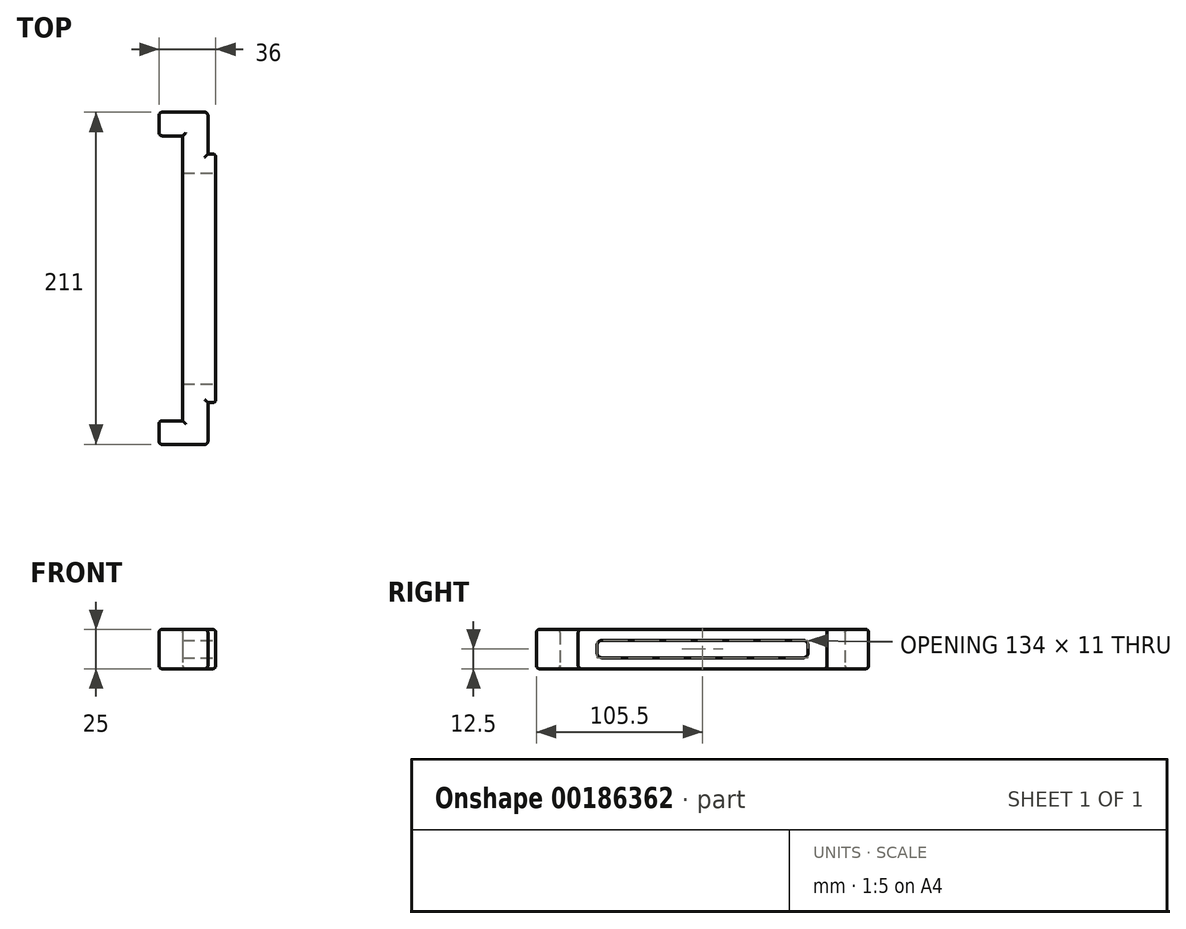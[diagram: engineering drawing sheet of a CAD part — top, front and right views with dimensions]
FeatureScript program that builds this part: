
annotation { "Feature Type Name" : "Feature", "Feature Type Description" : "" }
export const myFeature = defineFeature(function(context is Context, id is Id, definition is map)
    precondition{}
    {
        {
            var Q0;
            Q0=qCreatedBy(makeId("Top.planeOp"),FACE);
            var sketch = newSketch(context, id + "F0", { "sketchPlane" : qUnion([Q0])});
            skLineSegment(sketch, "E0", {"start": v(0, 90.5) * mm, "end": v(0, -90.5) * mm});
            skLineSegment(sketch, "E1", {"start": v(0, -90.5) * mm, "end": v(-15, -90.5) * mm});
            skLineSegment(sketch, "E2", {"start": v(-15, -90.5) * mm, "end": v(-15, -105.5) * mm});
            skLineSegment(sketch, "E3", {"start": v(-15, -105.5) * mm, "end": v(16, -105.5) * mm});
            skLineSegment(sketch, "E4", {"start": v(16, -105.5) * mm, "end": v(16, -79) * mm});
            skLineSegment(sketch, "E5", {"start": v(16, 105.5) * mm, "end": v(-15, 105.5) * mm});
            skLineSegment(sketch, "E6", {"start": v(-15, 105.5) * mm, "end": v(-15, 90.5) * mm});
            skLineSegment(sketch, "E7", {"start": v(-15, 90.5) * mm, "end": v(0, 90.5) * mm});
            skLineSegment(sketch, "E8", {"start": v(16, 79) * mm, "end": v(21, 79) * mm});
            skLineSegment(sketch, "E9", {"start": v(21, 79) * mm, "end": v(21, -79) * mm});
            skLineSegment(sketch, "E10", {"start": v(21, -79) * mm, "end": v(16, -79) * mm});
            skLineSegment(sketch, "E11.trimOffspring", {"start": v(16, 79) * mm, "end": v(16, 105.5) * mm});
            skSolve(sketch);
        }
        {
            var Q0;
            Q0=makeQuery(id+"F0.imprint","IMPRINT",FACE,{"disambiguationData":[TD([[makeQuery(id+"F0.imprint","IMPRINT",EDGE,{"derivedFrom":sQuery(id+"F0.wireOp",EDGE,"E0")}),1.0]])]});
            extrude(context, id + "F1", {"entities" : qUnion([Q0]), "depth" : 25 * mm});
        }
        {
            var Q0;
            Q0=makeQuery(id+"F1.opExtrude","SWEPT_EDGE",EDGE,{"disambiguationData":[OSD([sQuery(id+"F0.wireOp",EDGE,"E2"),sQuery(id+"F0.wireOp",EDGE,"E3")])]});
            var Q1;
            Q1=makeQuery(id+"F1.opExtrude","SWEPT_EDGE",EDGE,{"disambiguationData":[OSD([sQuery(id+"F0.wireOp",EDGE,"E5"),sQuery(id+"F0.wireOp",EDGE,"E6")])]});
            var Q2;
            Q2=makeQuery(id+"F1.opExtrude","SWEPT_EDGE",EDGE,{"disambiguationData":[OSD([sQuery(id+"F0.wireOp",EDGE,"E6"),sQuery(id+"F0.wireOp",EDGE,"E7")])]});
            var Q3;
            Q3=makeQuery(id+"F1.opExtrude","SWEPT_EDGE",EDGE,{"disambiguationData":[OSD([sQuery(id+"F0.wireOp",EDGE,"E1"),sQuery(id+"F0.wireOp",EDGE,"E2")])]});
            var Q4;
            Q4=makeQuery(id+"F1.opExtrude","SWEPT_EDGE",EDGE,{"disambiguationData":[OSD([sQuery(id+"F0.wireOp",EDGE,"E3"),sQuery(id+"F0.wireOp",EDGE,"E4")])]});
            var Q5;
            Q5=makeQuery(id+"F1.opExtrude","SWEPT_EDGE",EDGE,{"disambiguationData":[OSD([sQuery(id+"F0.wireOp",EDGE,"E9"),sQuery(id+"F0.wireOp",EDGE,"E10")])]});
            var Q6;
            Q6=makeQuery(id+"F1.opExtrude","SWEPT_EDGE",EDGE,{"disambiguationData":[OSD([sQuery(id+"F0.wireOp",EDGE,"E8"),sQuery(id+"F0.wireOp",EDGE,"E9")])]});
            var Q7;
            Q7=makeQuery(id+"F1.opExtrude","SWEPT_EDGE",EDGE,{"disambiguationData":[OSD([sQuery(id+"F0.wireOp",EDGE,"E5"),sQuery(id+"F0.wireOp",EDGE,"E11.trimOffspring")])]});
            fillet(context, id + "F2", {"entities" : qUnion([Q0, Q1, Q2, Q3, Q4, Q5, Q6, Q7]), "radius" : 2 * mm, "tangentPropagation" : true, "allowEdgeOverflow" : false});
        }
        {
            var Q0;
            Q0=makeQuery(id+"F1.opExtrude","SWEPT_FACE",FACE,{"disambiguationData":[OSD([sQuery(id+"F0.wireOp",EDGE,"E9")])]});
            var sketch = newSketch(context, id + "F3", { "sketchPlane" : qUnion([Q0])});
            skLineSegment(sketch, "E12.bottom", {"start": v(-67, 18) * mm, "end": v(67, 18) * mm});
            skLineSegment(sketch, "E12.top", {"start": v(-67, 7) * mm, "end": v(67, 7) * mm});
            skLineSegment(sketch, "E12.left", {"start": v(-67, 18) * mm, "end": v(-67, 7) * mm});
            skLineSegment(sketch, "E12.right", {"start": v(67, 18) * mm, "end": v(67, 7) * mm});
            skLineSegment(sketch, "E13", {"start": v(-67, 18) * mm, "end": v(-77, 25) * mm, "construction": true});
            skLineSegment(sketch, "E14", {"start": v(-67, 7) * mm, "end": v(-77, 0) * mm, "construction": true});
            skLineSegment(sketch, "E15", {"start": v(67, 18) * mm, "end": v(77, 25) * mm, "construction": true});
            skLineSegment(sketch, "E16", {"start": v(67, 7) * mm, "end": v(77, 0) * mm, "construction": true});
            skSolve(sketch);
        }
        {
            var Q0;
            Q0=makeQuery(id+"F3.imprint","IMPRINT",FACE,{"disambiguationData":[TD([[makeQuery(id+"F3.imprint","IMPRINT",EDGE,{"derivedFrom":sQuery(id+"F3.wireOp",EDGE,"E12.bottom")}),-1.0]])]});
            extrude(context, id + "F4", {"entities" : qUnion([Q0]), "operationType" : NewBodyOperationType.REMOVE, "oppositeDirection" : true, "depth" : 25 * mm});
        }
        {
            var Q0;
            Q0=makeQuery(id+"F4.boolean.opBoolean","COPY",EDGE,{"derivedFrom":makeQuery(id+"F4.opExtrude","SWEPT_EDGE",EDGE,{"disambiguationData":[OSD([sQuery(id+"F3.wireOp",EDGE,"E12.top"),sQuery(id+"F3.wireOp",EDGE,"E12.left")])]})});
            var Q1;
            Q1=makeQuery(id+"F4.boolean.opBoolean","COPY",EDGE,{"derivedFrom":makeQuery(id+"F4.opExtrude","SWEPT_EDGE",EDGE,{"disambiguationData":[OSD([sQuery(id+"F3.wireOp",EDGE,"E12.bottom"),sQuery(id+"F3.wireOp",EDGE,"E12.right")])]})});
            var Q2;
            Q2=makeQuery(id+"F4.boolean.opBoolean","COPY",EDGE,{"derivedFrom":makeQuery(id+"F4.opExtrude","SWEPT_EDGE",EDGE,{"disambiguationData":[OSD([sQuery(id+"F3.wireOp",EDGE,"E12.top"),sQuery(id+"F3.wireOp",EDGE,"E12.right")])]})});
            var Q3;
            Q3=makeQuery(id+"F4.boolean.opBoolean","COPY",EDGE,{"derivedFrom":makeQuery(id+"F4.opExtrude","SWEPT_EDGE",EDGE,{"disambiguationData":[OSD([sQuery(id+"F3.wireOp",EDGE,"E12.bottom"),sQuery(id+"F3.wireOp",EDGE,"E12.left")])]})});
            fillet(context, id + "F5", {"entities" : qUnion([Q0, Q1, Q2, Q3]), "radius" : 3 * mm, "tangentPropagation" : true, "allowEdgeOverflow" : false});
        }
        {
            var Q0;
            Q0=makeQuery(id+"F1.opExtrude","CAP_FACE",FACE,{"disambiguationData":[OSD([sQuery(id+"F0.wireOp",EDGE,"E0"),sQuery(id+"F0.wireOp",EDGE,"E1"),sQuery(id+"F0.wireOp",EDGE,"E2"),sQuery(id+"F0.wireOp",EDGE,"E3"),sQuery(id+"F0.wireOp",EDGE,"E4"),sQuery(id+"F0.wireOp",EDGE,"E5"),sQuery(id+"F0.wireOp",EDGE,"E6"),sQuery(id+"F0.wireOp",EDGE,"E7"),sQuery(id+"F0.wireOp",EDGE,"E8"),sQuery(id+"F0.wireOp",EDGE,"E9"),sQuery(id+"F0.wireOp",EDGE,"E10"),sQuery(id+"F0.wireOp",EDGE,"E11.trimOffspring")])],"isStart":false});
            var Q1;
            Q1=makeQuery(id+"F1.opExtrude","CAP_FACE",FACE,{"disambiguationData":[OSD([sQuery(id+"F0.wireOp",EDGE,"E0"),sQuery(id+"F0.wireOp",EDGE,"E1"),sQuery(id+"F0.wireOp",EDGE,"E2"),sQuery(id+"F0.wireOp",EDGE,"E3"),sQuery(id+"F0.wireOp",EDGE,"E4"),sQuery(id+"F0.wireOp",EDGE,"E5"),sQuery(id+"F0.wireOp",EDGE,"E6"),sQuery(id+"F0.wireOp",EDGE,"E7"),sQuery(id+"F0.wireOp",EDGE,"E8"),sQuery(id+"F0.wireOp",EDGE,"E9"),sQuery(id+"F0.wireOp",EDGE,"E10"),sQuery(id+"F0.wireOp",EDGE,"E11.trimOffspring")])],"isStart":true});
            fillet(context, id + "F6", {"entities" : qUnion([Q0, Q1]), "radius" : 2 * mm, "tangentPropagation" : true, "allowEdgeOverflow" : false});
        }
    });
